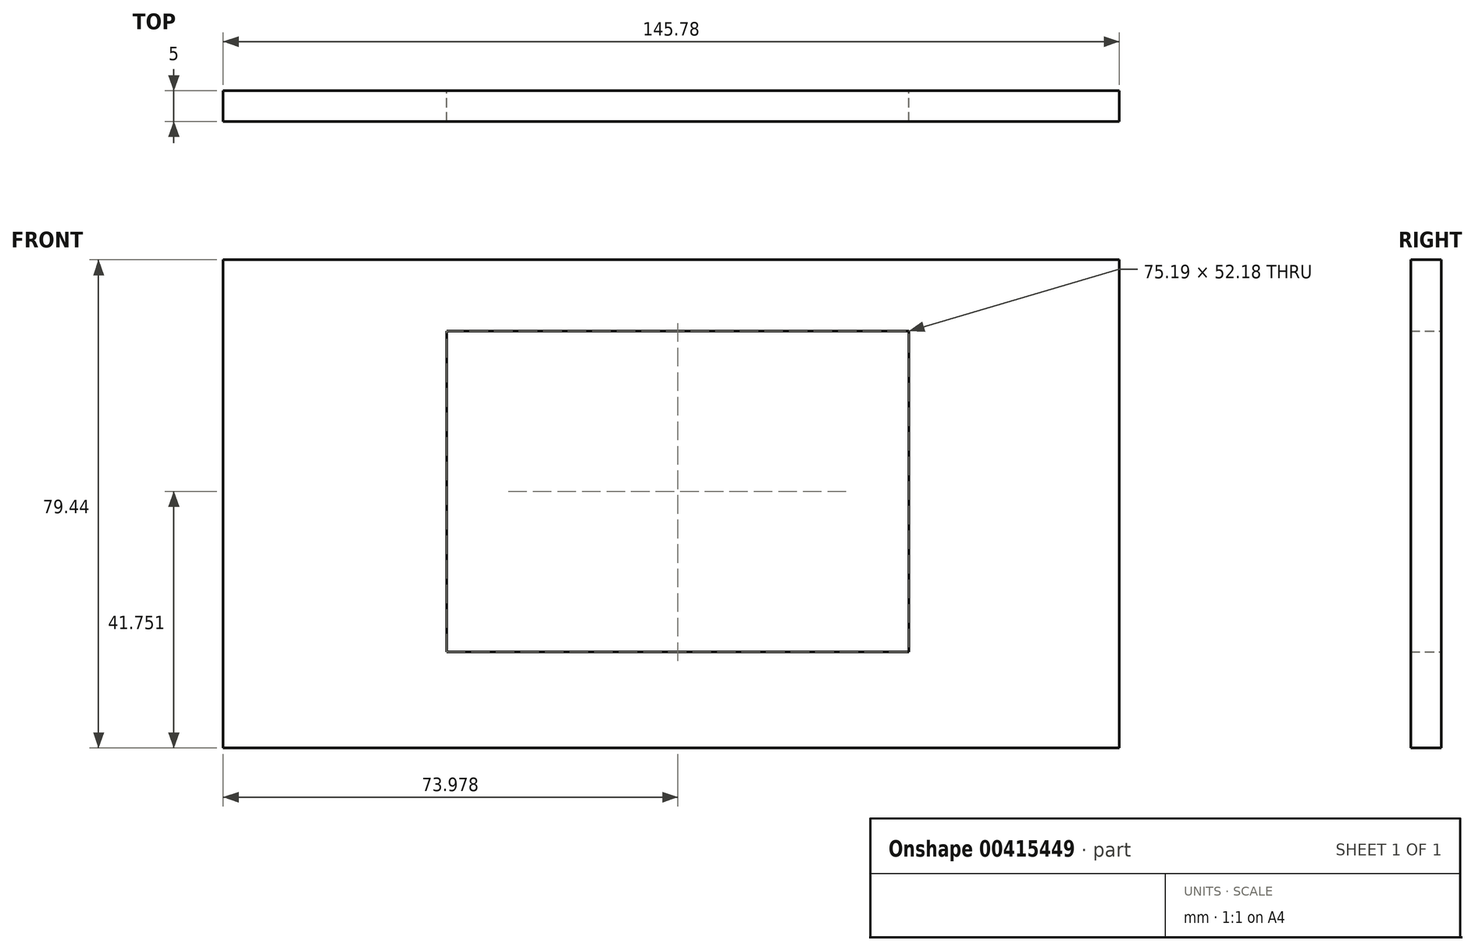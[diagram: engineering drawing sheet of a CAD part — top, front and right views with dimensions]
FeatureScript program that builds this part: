
annotation { "Feature Type Name" : "Feature", "Feature Type Description" : "" }
export const myFeature = defineFeature(function(context is Context, id is Id, definition is map)
    precondition{}
    {
        {
            var Q0;
            Q0=qCreatedBy(makeId("Front.planeOp"),FACE);
            var sketch = newSketch(context, id + "F0", { "sketchPlane" : qUnion([Q0])});
            skLineSegment(sketch, "E0.bottom", {"start": v(72.89, 39.72) * mm, "end": v(-72.89, 39.72) * mm});
            skLineSegment(sketch, "E0.top", {"start": v(72.89, -39.72) * mm, "end": v(-72.89, -39.72) * mm});
            skLineSegment(sketch, "E0.left", {"start": v(72.89, 39.72) * mm, "end": v(72.89, -39.72) * mm});
            skLineSegment(sketch, "E0.right", {"start": v(-72.89, 39.72) * mm, "end": v(-72.89, -39.72) * mm});
            skPoint(sketch, "E0.middle", {"position": v(0, 0) * mm});
            skLineSegment(sketch, "E1.bottom", {"start": v(-36.5, 28.12) * mm, "end": v(38.68, 28.12) * mm});
            skLineSegment(sketch, "E1.top", {"start": v(-36.5, -24.06) * mm, "end": v(38.68, -24.06) * mm});
            skLineSegment(sketch, "E1.left", {"start": v(-36.5, 28.12) * mm, "end": v(-36.5, -24.06) * mm});
            skLineSegment(sketch, "E1.right", {"start": v(38.68, 28.12) * mm, "end": v(38.68, -24.06) * mm});
            skSolve(sketch);
        }
        {
            var Q0;
            Q0=makeQuery(id+"F0.imprint","IMPRINT",FACE,{"disambiguationData":[TD([[makeQuery(id+"F0.imprint","IMPRINT",EDGE,{"derivedFrom":sQuery(id+"F0.wireOp",EDGE,"E0.bottom")}),1.0]])]});
            extrude(context, id + "F1", {"entities" : qUnion([Q0]), "endBound" : BoundingType.SYMMETRIC, "depth" : 5 * mm});
        }
    });
